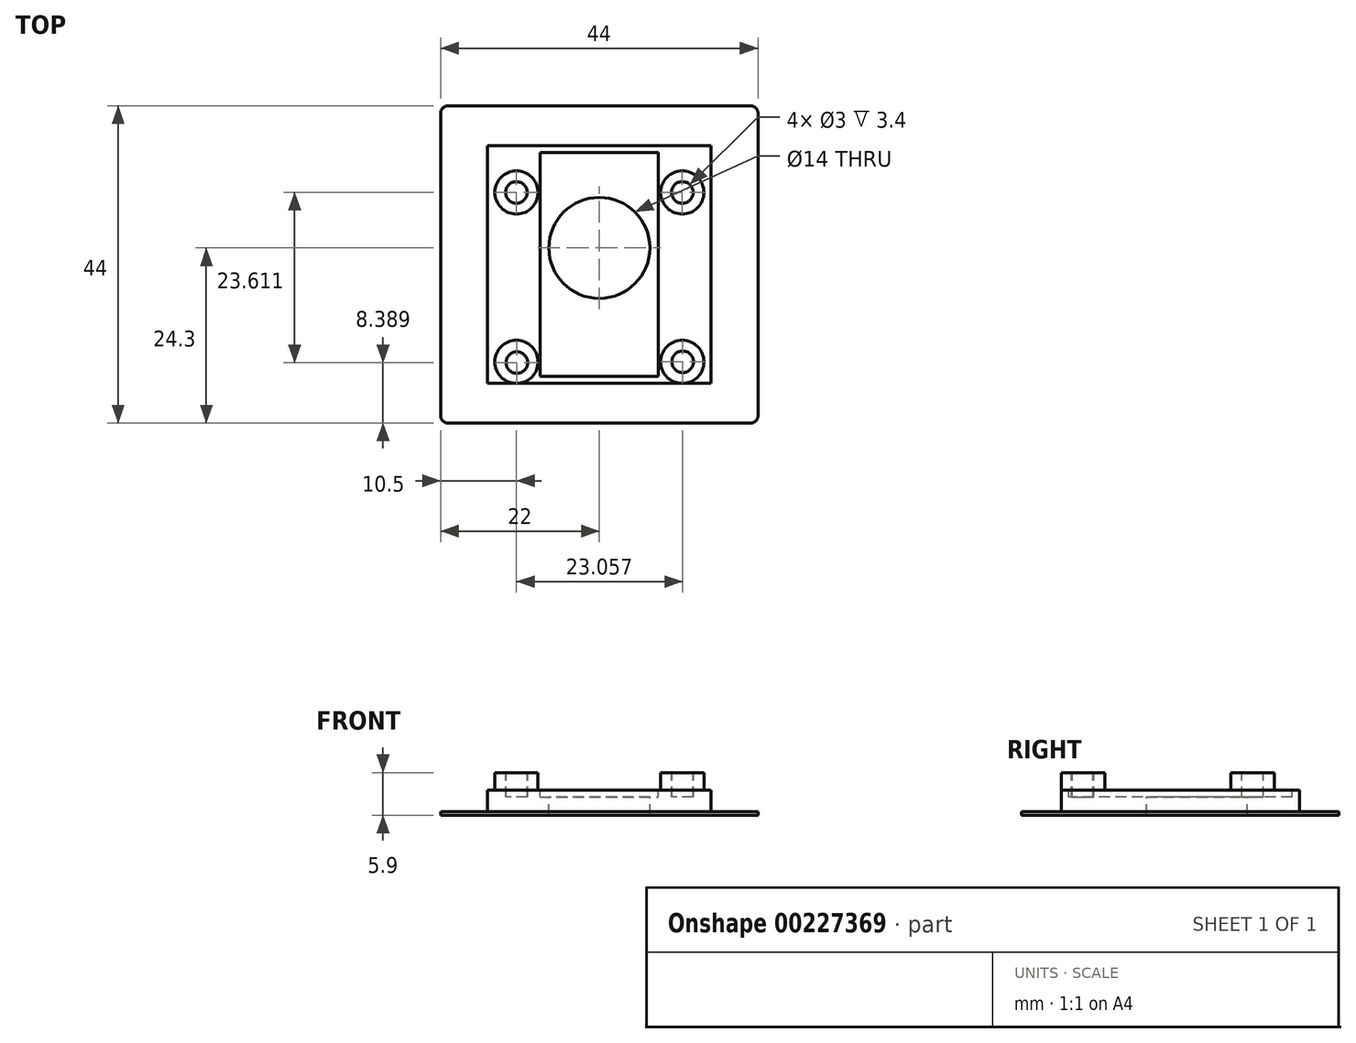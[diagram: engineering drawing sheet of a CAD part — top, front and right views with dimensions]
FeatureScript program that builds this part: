
annotation { "Feature Type Name" : "Feature", "Feature Type Description" : "" }
export const myFeature = defineFeature(function(context is Context, id is Id, definition is map)
    precondition{}
    {
        {
            var Q0;
            Q0=qCreatedBy(makeId("Top.planeOp"),FACE);
            var sketch = newSketch(context, id + "F0", { "sketchPlane" : qUnion([Q0])});
            skLineSegment(sketch, "E0.bottom", {"start": v(0, 0) * mm, "end": v(31, 0) * mm});
            skLineSegment(sketch, "E0.top", {"start": v(0, 33) * mm, "end": v(31, 33) * mm});
            skLineSegment(sketch, "E0.left", {"start": v(0, 0) * mm, "end": v(0, 33) * mm});
            skLineSegment(sketch, "E0.right", {"start": v(31, 0) * mm, "end": v(31, 33) * mm});
            skSolve(sketch);
        }
        {
            var Q0;
            Q0 = qSketchRegion(id + "F0", true);
            extrude(context, id + "F1", {"entities" : qUnion([Q0]), "depth" : 2 * mm});
        }
        {
            var Q0;
            Q0=makeQuery(id+"F1.opExtrude","CAP_FACE",FACE,{"disambiguationData":[OSD([sQuery(id+"F0.wireOp",EDGE,"E0.bottom"),sQuery(id+"F0.wireOp",EDGE,"E0.top"),sQuery(id+"F0.wireOp",EDGE,"E0.left"),sQuery(id+"F0.wireOp",EDGE,"E0.right")])],"isStart":false});
            var sketch = newSketch(context, id + "F2", { "sketchPlane" : qUnion([Q0])});
            skCircle(sketch, "E1", {"center": v(4, 3) * mm, "radius": 3 * mm});
            skCircle(sketch, "E2", {"center": v(4, 26.5) * mm, "radius": 3 * mm});
            skCircle(sketch, "E3", {"center": v(27, 26.5) * mm, "radius": 3 * mm});
            skCircle(sketch, "E4", {"center": v(27, 3) * mm, "radius": 3 * mm});
            skSolve(sketch);
        }
        {
            var Q0;
            Q0 = qSketchRegion(id + "F2", true);
            extrude(context, id + "F3", {"entities" : qUnion([Q0]), "operationType" : NewBodyOperationType.ADD, "depth" : 2.4 * mm});
        }
        {
            var Q0;
            Q0=makeQuery(id+"F1.opExtrude","CAP_FACE",FACE,{"disambiguationData":[OSD([sQuery(id+"F0.wireOp",EDGE,"E0.bottom"),sQuery(id+"F0.wireOp",EDGE,"E0.top"),sQuery(id+"F0.wireOp",EDGE,"E0.left"),sQuery(id+"F0.wireOp",EDGE,"E0.right")])],"isStart":false});
            var sketch = newSketch(context, id + "F4", { "sketchPlane" : qUnion([Q0])});
            skLineSegment(sketch, "E5.bottom", {"start": v(7.3, 32) * mm, "end": v(23.7, 32) * mm});
            skLineSegment(sketch, "E5.top", {"start": v(7.3, 1) * mm, "end": v(23.7, 1) * mm});
            skLineSegment(sketch, "E5.left", {"start": v(7.3, 32) * mm, "end": v(7.3, 1) * mm});
            skLineSegment(sketch, "E5.right", {"start": v(23.7, 32) * mm, "end": v(23.7, 1) * mm});
            skSolve(sketch);
        }
        {
            var Q0;
            Q0=makeQuery(id+"F4.imprint","IMPRINT",FACE,{"disambiguationData":[TD([[makeQuery(id+"F4.imprint","IMPRINT",EDGE,{"derivedFrom":sQuery(id+"F4.wireOp",EDGE,"E5.bottom")}),-1.0]])]});
            extrude(context, id + "F5", {"entities" : qUnion([Q0]), "operationType" : NewBodyOperationType.REMOVE, "oppositeDirection" : true, "depth" : 1 * mm});
        }
        {
            var Q0;
            Q0=makeQuery(id+"F3.opExtrude","CAP_FACE",FACE,{"disambiguationData":[OSD([sQuery(id+"F2.wireOp",EDGE,"E3")])],"isStart":false});
            var sketch = newSketch(context, id + "F6", { "sketchPlane" : qUnion([Q0])});
            skCircle(sketch, "E6", {"center": v(27, 26.5) * mm, "radius": 1.5 * mm});
            skSolve(sketch);
        }
        {
            var Q0;
            Q0 = qSketchRegion(id + "F6", true);
            extrude(context, id + "F7", {"entities" : qUnion([Q0]), "operationType" : NewBodyOperationType.REMOVE, "oppositeDirection" : true, "depth" : 3.4 * mm});
        }
        {
            var Q0;
            Q0=makeQuery(id+"F3.opExtrude","CAP_FACE",FACE,{"disambiguationData":[OSD([sQuery(id+"F2.wireOp",EDGE,"E2")])],"isStart":false});
            var sketch = newSketch(context, id + "F8", { "sketchPlane" : qUnion([Q0])});
            skCircle(sketch, "E7", {"center": v(4, 26.5) * mm, "radius": 1.5 * mm});
            skCircle(sketch, "E8", {"center": v(4.06, 2.89) * mm, "radius": 1.5 * mm});
            skCircle(sketch, "E9", {"center": v(27.06, 3) * mm, "radius": 1.5 * mm});
            skSolve(sketch);
        }
        {
            var Q0;
            Q0=makeQuery(id+"F8.imprint","IMPRINT",FACE,{"disambiguationData":[TD([[makeQuery(id+"F8.imprint","IMPRINT",EDGE,{"derivedFrom":sQuery(id+"F8.wireOp",EDGE,"E7")}),1.0]])]});
            var Q1;
            Q1=makeQuery(id+"F8.imprint","IMPRINT",FACE,{"disambiguationData":[TD([[makeQuery(id+"F8.imprint","IMPRINT",EDGE,{"derivedFrom":sQuery(id+"F8.wireOp",EDGE,"E8")}),1.0]])]});
            var Q2;
            Q2=makeQuery(id+"F8.imprint","IMPRINT",FACE,{"disambiguationData":[TD([[makeQuery(id+"F8.imprint","IMPRINT",EDGE,{"derivedFrom":sQuery(id+"F8.wireOp",EDGE,"E9")}),1.0]])]});
            extrude(context, id + "F9", {"entities" : qUnion([Q0, Q1, Q2]), "operationType" : NewBodyOperationType.REMOVE, "oppositeDirection" : true, "depth" : 3.4 * mm});
        }
        {
            var Q0;
            Q0=makeQuery(id+"F5.boolean.opBoolean","COPY",FACE,{"derivedFrom":makeQuery(id+"F5.opExtrude","CAP_FACE",FACE,{"disambiguationData":[OSD([sQuery(id+"F4.wireOp",EDGE,"E5.bottom"),sQuery(id+"F4.wireOp",EDGE,"E5.top"),sQuery(id+"F4.wireOp",EDGE,"E5.left"),sQuery(id+"F4.wireOp",EDGE,"E5.right")])],"isStart":false})});
            var sketch = newSketch(context, id + "F10", { "sketchPlane" : qUnion([Q0])});
            skCircle(sketch, "E10", {"center": v(15.5, 18.8) * mm, "radius": 7 * mm});
            skSolve(sketch);
        }
        {
            var Q0;
            Q0 = qSketchRegion(id + "F10", true);
            extrude(context, id + "F11", {"entities" : qUnion([Q0]), "operationType" : NewBodyOperationType.REMOVE, "oppositeDirection" : true, "depth" : 25 * mm});
        }
        {
            var Q0;
            Q0=makeQuery(id+"F1.opExtrude","CAP_FACE",FACE,{"disambiguationData":[OSD([sQuery(id+"F0.wireOp",EDGE,"E0.bottom"),sQuery(id+"F0.wireOp",EDGE,"E0.top"),sQuery(id+"F0.wireOp",EDGE,"E0.left"),sQuery(id+"F0.wireOp",EDGE,"E0.right")])],"isStart":true});
            extrude(context, id + "F12", {"entities" : qUnion([Q0]), "operationType" : NewBodyOperationType.ADD, "depth" : 1 * mm});
        }
        {
            var Q0;
            Q0=makeQuery(id+"F12.opExtrude","CAP_FACE",FACE,{"disambiguationData":[OSD([sQuery(id+"F0.wireOp",EDGE,"E0.bottom"),sQuery(id+"F0.wireOp",EDGE,"E0.top"),sQuery(id+"F0.wireOp",EDGE,"E0.left"),sQuery(id+"F0.wireOp",EDGE,"E0.right")])],"isStart":false});
            var sketch = newSketch(context, id + "F13", { "sketchPlane" : qUnion([Q0])});
            skLineSegment(sketch, "E11.bottom", {"start": v(-6.5, 5.5) * mm, "end": v(37.5, 5.5) * mm});
            skLineSegment(sketch, "E11.top", {"start": v(-6.5, -38.5) * mm, "end": v(37.5, -38.5) * mm});
            skLineSegment(sketch, "E11.left", {"start": v(-6.5, 5.5) * mm, "end": v(-6.5, -38.5) * mm});
            skLineSegment(sketch, "E11.right", {"start": v(37.5, 5.5) * mm, "end": v(37.5, -38.5) * mm});
            skSolve(sketch);
        }
        {
            var Q0;
            Q0=makeQuery(id+"F13.imprint","IMPRINT",FACE,{"disambiguationData":[TD([[makeQuery(id+"F13.imprint","IMPRINT",EDGE,{"derivedFrom":sQuery(id+"F13.wireOp",EDGE,"E11.bottom")}),-1.0]])]});
            var Q1;
            {var subQ3=sQuery(id+"F0.wireOp",EDGE,"E0.bottom");Q1=makeQuery(id+"F13.imprint","IMPRINT",FACE,{"disambiguationData":[TD([[makeQuery(id+"F13.imprint","IMPRINT",EDGE,{"derivedFrom":makeQuery(id+"F12.opExtrude","CAP_EDGE",EDGE,{"disambiguationData":[OSD([subQ3])],"isStart":false})}),-1.0]])]});}
            extrude(context, id + "F14", {"entities" : qUnion([Q0, Q1]), "operationType" : NewBodyOperationType.ADD, "depth" : 0.5 * mm});
        }
        {
            var Q0;
            Q0=makeQuery(id+"F14.opExtrude","SWEPT_EDGE",EDGE,{"disambiguationData":[OSD([sQuery(id+"F13.wireOp",EDGE,"E11.bottom"),sQuery(id+"F13.wireOp",EDGE,"E11.left")])]});
            var Q1;
            Q1=makeQuery(id+"F14.opExtrude","SWEPT_EDGE",EDGE,{"disambiguationData":[OSD([sQuery(id+"F13.wireOp",EDGE,"E11.bottom"),sQuery(id+"F13.wireOp",EDGE,"E11.right")])]});
            var Q2;
            Q2=makeQuery(id+"F14.opExtrude","SWEPT_EDGE",EDGE,{"disambiguationData":[OSD([sQuery(id+"F13.wireOp",EDGE,"E11.top"),sQuery(id+"F13.wireOp",EDGE,"E11.right")])]});
            var Q3;
            Q3=makeQuery(id+"F14.opExtrude","SWEPT_EDGE",EDGE,{"disambiguationData":[OSD([sQuery(id+"F13.wireOp",EDGE,"E11.top"),sQuery(id+"F13.wireOp",EDGE,"E11.left")])]});
            fillet(context, id + "F15", {"entities" : qUnion([Q0, Q1, Q2, Q3]), "radius" : 1 * mm, "tangentPropagation" : true, "allowEdgeOverflow" : false});
        }
    });
